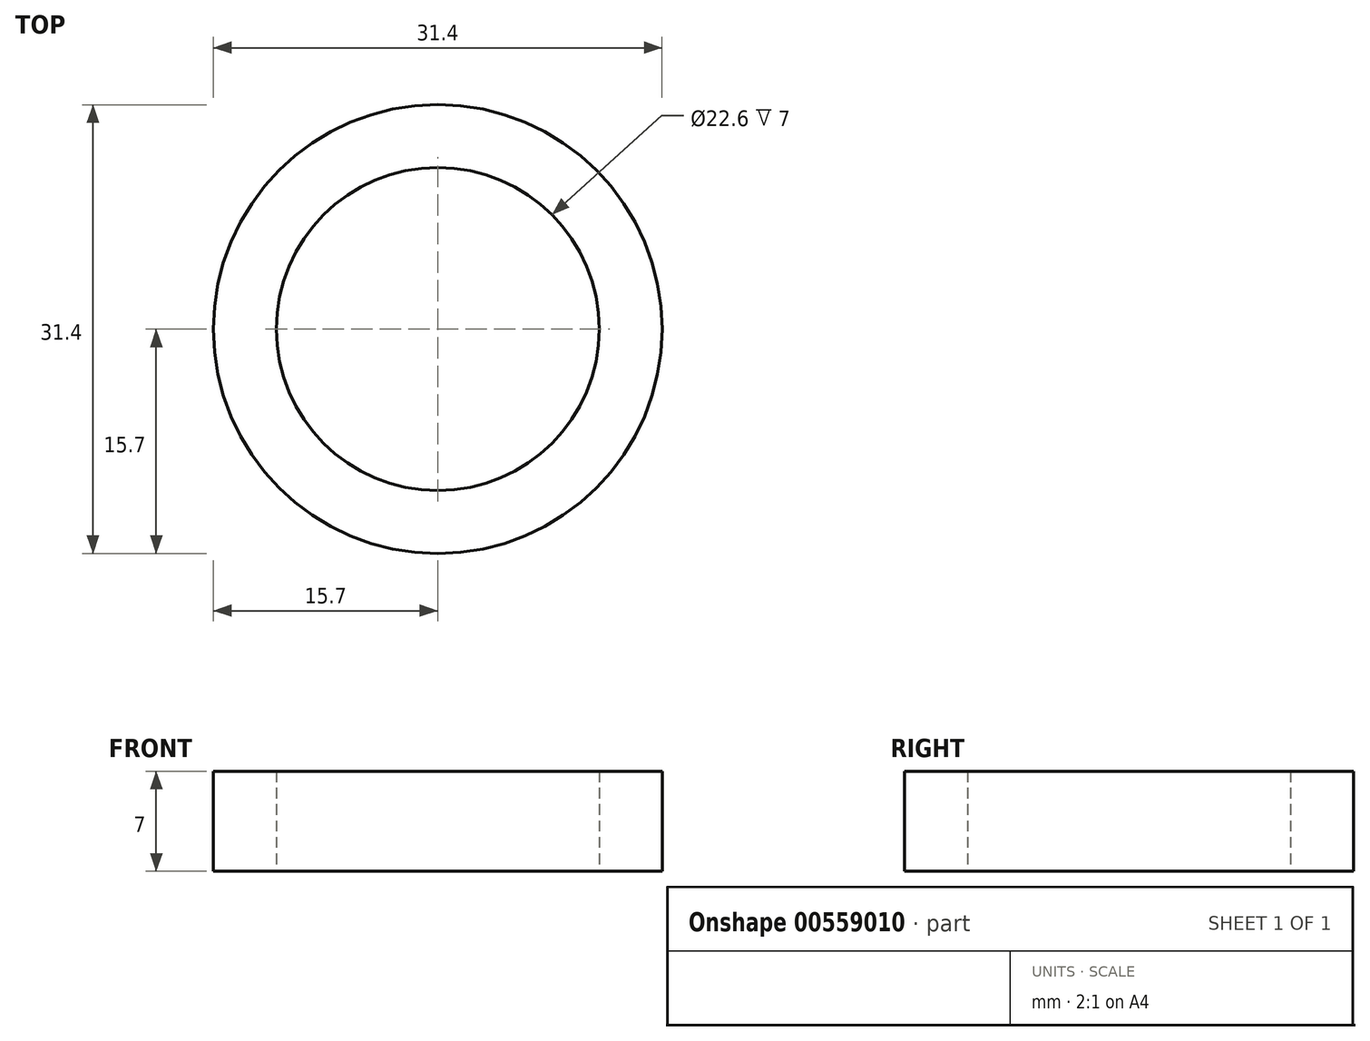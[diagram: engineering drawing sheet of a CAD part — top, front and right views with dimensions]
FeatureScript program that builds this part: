
annotation { "Feature Type Name" : "Feature", "Feature Type Description" : "" }
export const myFeature = defineFeature(function(context is Context, id is Id, definition is map)
    precondition{}
    {
        {
            var Q0;
            Q0=qCreatedBy(makeId("Top.planeOp"),FACE);
            var sketch = newSketch(context, id + "F0", { "sketchPlane" : qUnion([Q0])});
            skCircle(sketch, "E0", {"center": v(0, 0) * mm, "radius": 11.3 * mm});
            skCircle(sketch, "E1", {"center": v(0, 0) * mm, "radius": 15.7 * mm});
            skSolve(sketch);
        }
        {
            var Q0;
            Q0=makeQuery(id+"F0.imprint","IMPRINT",FACE,{"disambiguationData":[TD([[makeQuery(id+"F0.imprint","IMPRINT",EDGE,{"derivedFrom":sQuery(id+"F0.wireOp",EDGE,"E0")}),-1.0]])]});
            extrude(context, id + "F1", {"entities" : qUnion([Q0]), "depth" : 7 * mm, "offsetDistance" : 25 * mm});
        }
    });
